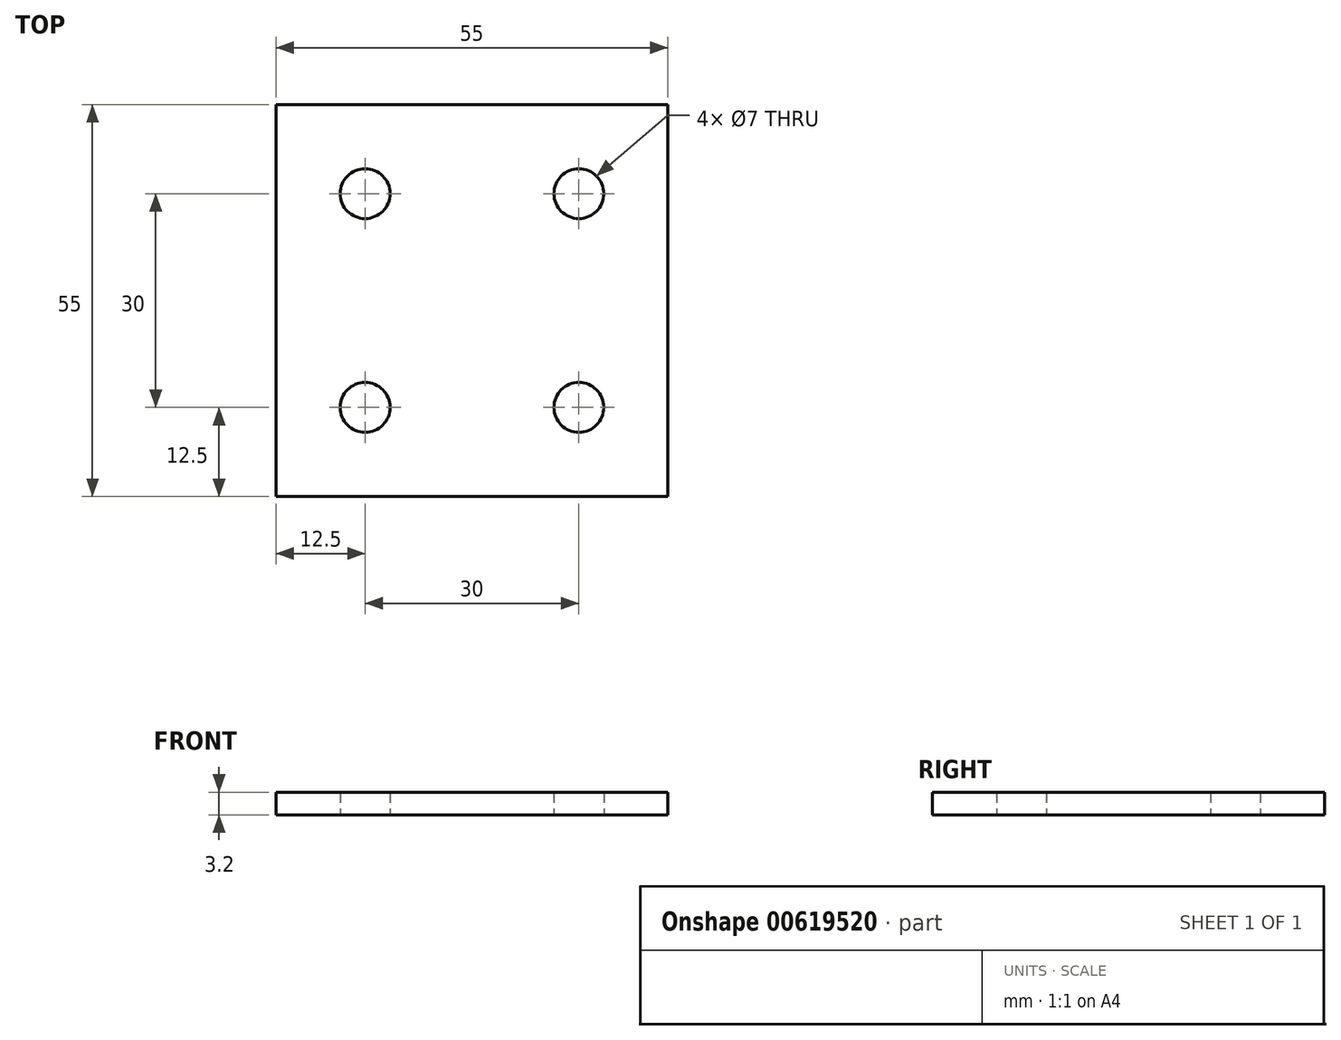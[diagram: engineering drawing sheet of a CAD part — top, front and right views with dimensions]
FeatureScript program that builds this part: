
annotation { "Feature Type Name" : "Feature", "Feature Type Description" : "" }
export const myFeature = defineFeature(function(context is Context, id is Id, definition is map)
    precondition{}
    {
        {
            var Q0;
            Q0=qCreatedBy(makeId("Top.planeOp"),FACE);
            var sketch = newSketch(context, id + "F0", { "sketchPlane" : qUnion([Q0])});
            skLineSegment(sketch, "E0.bottom", {"start": v(27.5, 27.5) * mm, "end": v(-27.5, 27.5) * mm});
            skLineSegment(sketch, "E0.top", {"start": v(27.5, -27.5) * mm, "end": v(-27.5, -27.5) * mm});
            skLineSegment(sketch, "E0.left", {"start": v(27.5, 27.5) * mm, "end": v(27.5, -27.5) * mm});
            skLineSegment(sketch, "E0.right", {"start": v(-27.5, 27.5) * mm, "end": v(-27.5, -27.5) * mm});
            skPoint(sketch, "E0.middle", {"position": v(0, 0) * mm});
            skCircle(sketch, "E1", {"center": v(-15, 15) * mm, "radius": 3.5 * mm});
            skCircle(sketch, "E2", {"center": v(15, 15) * mm, "radius": 3.5 * mm});
            skCircle(sketch, "E3", {"center": v(15, -15) * mm, "radius": 3.5 * mm});
            skCircle(sketch, "E4", {"center": v(-15, -15) * mm, "radius": 3.5 * mm});
            skSolve(sketch);
        }
        {
            var Q0;
            Q0=qSketchRegion(id+"F0",true);
            extrude(context, id + "F1", {"entities" : qUnion([Q0]), "depth" : 3.2 * mm, "offsetDistance" : 25 * mm});
        }
    });
